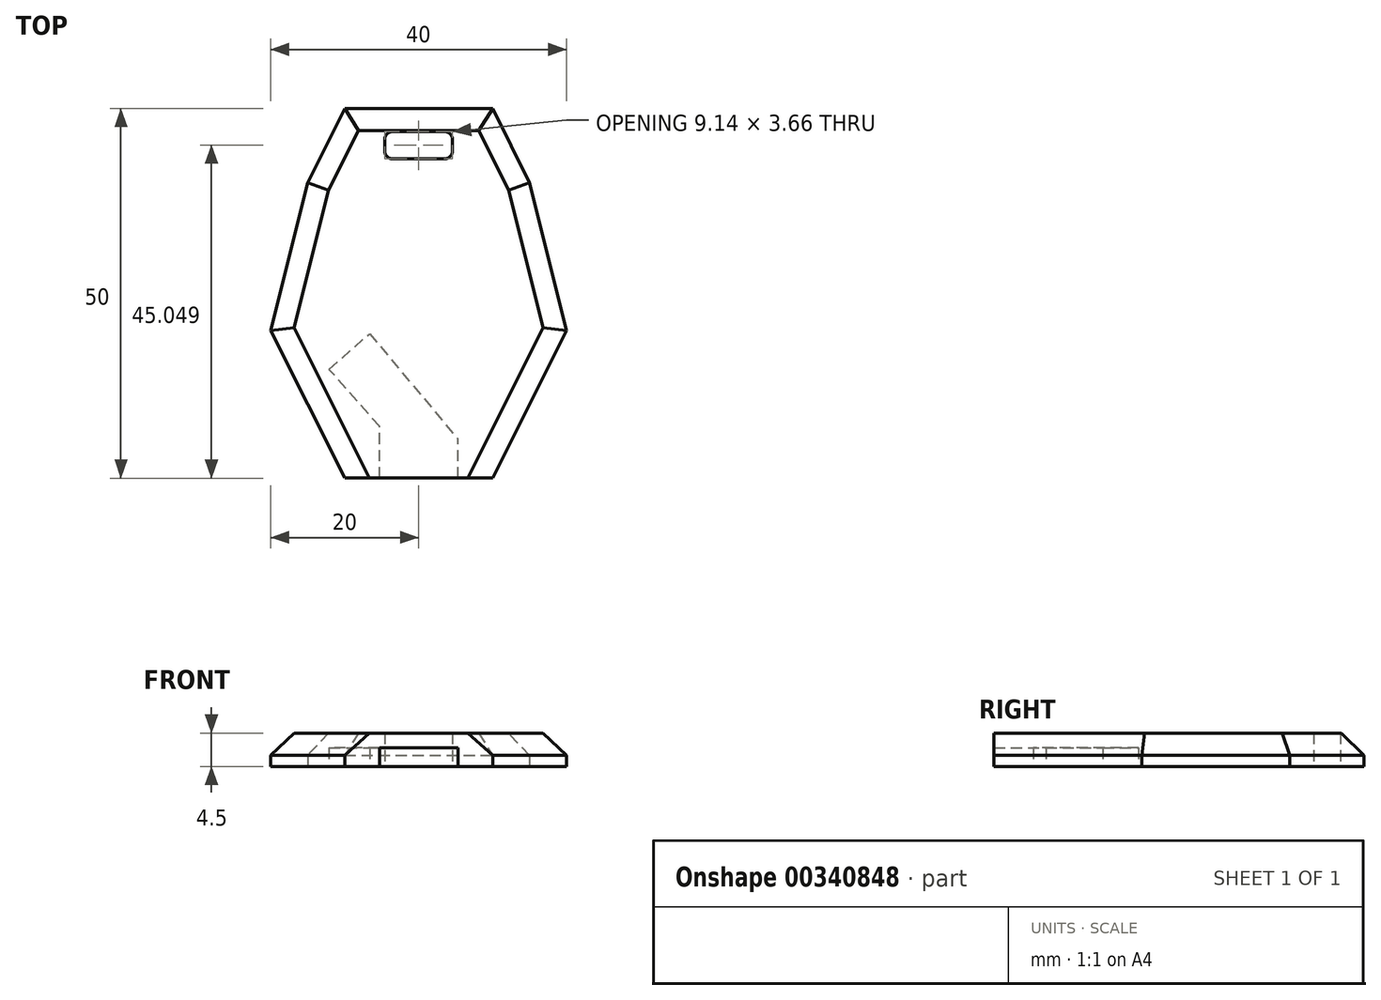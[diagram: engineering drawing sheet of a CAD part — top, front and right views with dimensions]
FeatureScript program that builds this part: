
annotation { "Feature Type Name" : "Feature", "Feature Type Description" : "" }
export const myFeature = defineFeature(function(context is Context, id is Id, definition is map)
    precondition{}
    {
        {
            var Q0;
            Q0=qCreatedBy(makeId("Top.planeOp"),FACE);
            var sketch = newSketch(context, id + "F0", { "sketchPlane" : qUnion([Q0])});
            skLineSegment(sketch, "E0", {"start": v(-10, 54.98) * mm, "end": v(10, 54.98) * mm});
            skLineSegment(sketch, "E1", {"start": v(-10, 4.98) * mm, "end": v(10, 4.98) * mm});
            skLineSegment(sketch, "E2", {"start": v(-10, 54.98) * mm, "end": v(-15, 44.98) * mm});
            skLineSegment(sketch, "E3", {"start": v(-20, 24.98) * mm, "end": v(-15, 44.98) * mm});
            skLineSegment(sketch, "E4", {"start": v(-10, 4.98) * mm, "end": v(-20, 24.98) * mm});
            skLineSegment(sketch, "E5", {"start": v(10, 4.98) * mm, "end": v(20, 24.98) * mm});
            skLineSegment(sketch, "E6", {"start": v(20, 24.98) * mm, "end": v(15, 44.98) * mm});
            skLineSegment(sketch, "E7", {"start": v(15, 44.98) * mm, "end": v(10, 54.98) * mm});
            skLineSegment(sketch, "E8", {"start": v(-5.3, 4.98) * mm, "end": v(-5.3, 11.98) * mm});
            skLineSegment(sketch, "E9", {"start": v(5.3, 4.98) * mm, "end": v(5.3, 10.28) * mm});
            skLineSegment(sketch, "E10", {"start": v(-5.3, 11.98) * mm, "end": v(-12.1, 19.71) * mm});
            skLineSegment(sketch, "E11", {"start": v(-12.1, 19.71) * mm, "end": v(-6.63, 24.54) * mm});
            skLineSegment(sketch, "E12", {"start": v(-6.63, 24.54) * mm, "end": v(5.3, 10.28) * mm});
            skLineSegment(sketch, "E13.bottom", {"start": v(-4.57, 51.86) * mm, "end": v(4.57, 51.86) * mm});
            skLineSegment(sketch, "E13.top", {"start": v(-4.57, 48.2) * mm, "end": v(4.57, 48.2) * mm});
            skLineSegment(sketch, "E13.left", {"start": v(-4.57, 51.86) * mm, "end": v(-4.57, 48.2) * mm});
            skLineSegment(sketch, "E13.right", {"start": v(4.57, 51.86) * mm, "end": v(4.57, 48.2) * mm});
            skSolve(sketch);
        }
        {
            var Q0;
            Q0=makeQuery(id+"F0.imprint","IMPRINT",FACE,{"disambiguationData":[TD([[makeQuery(id+"F0.imprint","IMPRINT",EDGE,{"derivedFrom":sQuery(id+"F0.wireOp",EDGE,"E0")}),-1.0]])]});
            extrude(context, id + "F1", {"entities" : qUnion([Q0]), "depth" : 4.5 * mm});
        }
        {
            var Q0;
            Q0=makeQuery(id+"F1.opExtrude","CAP_FACE",FACE,{"disambiguationData":[OSD([sQuery(id+"F0.wireOp",EDGE,"E0"),sQuery(id+"F0.wireOp",EDGE,"E1"),sQuery(id+"F0.wireOp",EDGE,"E2"),sQuery(id+"F0.wireOp",EDGE,"E3"),sQuery(id+"F0.wireOp",EDGE,"E4"),sQuery(id+"F0.wireOp",EDGE,"E5"),sQuery(id+"F0.wireOp",EDGE,"E6"),sQuery(id+"F0.wireOp",EDGE,"E7"),sQuery(id+"F0.wireOp",EDGE,"E8"),sQuery(id+"F0.wireOp",EDGE,"E9"),sQuery(id+"F0.wireOp",EDGE,"E10"),sQuery(id+"F0.wireOp",EDGE,"E11"),sQuery(id+"F0.wireOp",EDGE,"E12"),sQuery(id+"F0.wireOp",EDGE,"E13.bottom"),sQuery(id+"F0.wireOp",EDGE,"E13.top"),sQuery(id+"F0.wireOp",EDGE,"E13.left"),sQuery(id+"F0.wireOp",EDGE,"E13.right")])],"isStart":false});
            var sketch = newSketch(context, id + "F2", { "sketchPlane" : qUnion([Q0])});
            skLineSegment(sketch, "E14", {"start": v(-5.3, 4.98) * mm, "end": v(5.3, 4.98) * mm});
            skSolve(sketch);
        }
        {
            var Q0;
            Q0=makeQuery(id+"F2.imprint","IMPRINT",FACE,{"disambiguationData":[TD([[makeQuery(id+"F2.imprint","IMPRINT",EDGE,{"derivedFrom":sQuery(id+"F2.wireOp",EDGE,"E14")}),1.0]])]});
            extrude(context, id + "F3", {"entities" : qUnion([Q0]), "operationType" : NewBodyOperationType.ADD, "oppositeDirection" : true, "depth" : 2 * mm});
        }
        {
            var Q0;
            Q0=makeQuery(id+"F1.opExtrude","CAP_EDGE",EDGE,{"disambiguationData":[OSD([sQuery(id+"F0.wireOp",EDGE,"E4")])],"isStart":false});
            var Q1;
            Q1=makeQuery(id+"F1.opExtrude","CAP_EDGE",EDGE,{"disambiguationData":[OSD([sQuery(id+"F0.wireOp",EDGE,"E3")])],"isStart":false});
            var Q2;
            Q2=makeQuery(id+"F1.opExtrude","CAP_EDGE",EDGE,{"disambiguationData":[OSD([sQuery(id+"F0.wireOp",EDGE,"E0")])],"isStart":false});
            var Q3;
            Q3=makeQuery(id+"F1.opExtrude","CAP_EDGE",EDGE,{"disambiguationData":[OSD([sQuery(id+"F0.wireOp",EDGE,"E7")])],"isStart":false});
            var Q4;
            Q4=makeQuery(id+"F1.opExtrude","CAP_EDGE",EDGE,{"disambiguationData":[OSD([sQuery(id+"F0.wireOp",EDGE,"E6")])],"isStart":false});
            var Q5;
            Q5=makeQuery(id+"F1.opExtrude","CAP_EDGE",EDGE,{"disambiguationData":[OSD([sQuery(id+"F0.wireOp",EDGE,"E5")])],"isStart":false});
            var Q6;
            Q6=makeQuery(id+"F1.opExtrude","CAP_EDGE",EDGE,{"disambiguationData":[OSD([sQuery(id+"F0.wireOp",EDGE,"E2")])],"isStart":false});
            chamfer(context, id + "F4", {"entities" : qUnion([Q0, Q1, Q2, Q3, Q4, Q5, Q6]), "width" : 3 * mm, "tangentPropagation" : true});
        }
        {
            var Q0;
            Q0=makeQuery(id+"F1.opExtrude","SWEPT_EDGE",EDGE,{"disambiguationData":[OSD([sQuery(id+"F0.wireOp",EDGE,"E13.top"),sQuery(id+"F0.wireOp",EDGE,"E13.left")])]});
            var Q1;
            Q1=makeQuery(id+"F1.opExtrude","SWEPT_EDGE",EDGE,{"disambiguationData":[OSD([sQuery(id+"F0.wireOp",EDGE,"E13.bottom"),sQuery(id+"F0.wireOp",EDGE,"E13.left")])]});
            var Q2;
            Q2=makeQuery(id+"F1.opExtrude","SWEPT_EDGE",EDGE,{"disambiguationData":[OSD([sQuery(id+"F0.wireOp",EDGE,"E13.bottom"),sQuery(id+"F0.wireOp",EDGE,"E13.right")])]});
            var Q3;
            Q3=makeQuery(id+"F1.opExtrude","SWEPT_EDGE",EDGE,{"disambiguationData":[OSD([sQuery(id+"F0.wireOp",EDGE,"E13.top"),sQuery(id+"F0.wireOp",EDGE,"E13.right")])]});
            fillet(context, id + "F5", {"entities" : qUnion([Q0, Q1, Q2, Q3]), "radius" : 1 * mm, "tangentPropagation" : true, "allowEdgeOverflow" : false});
        }
    });
